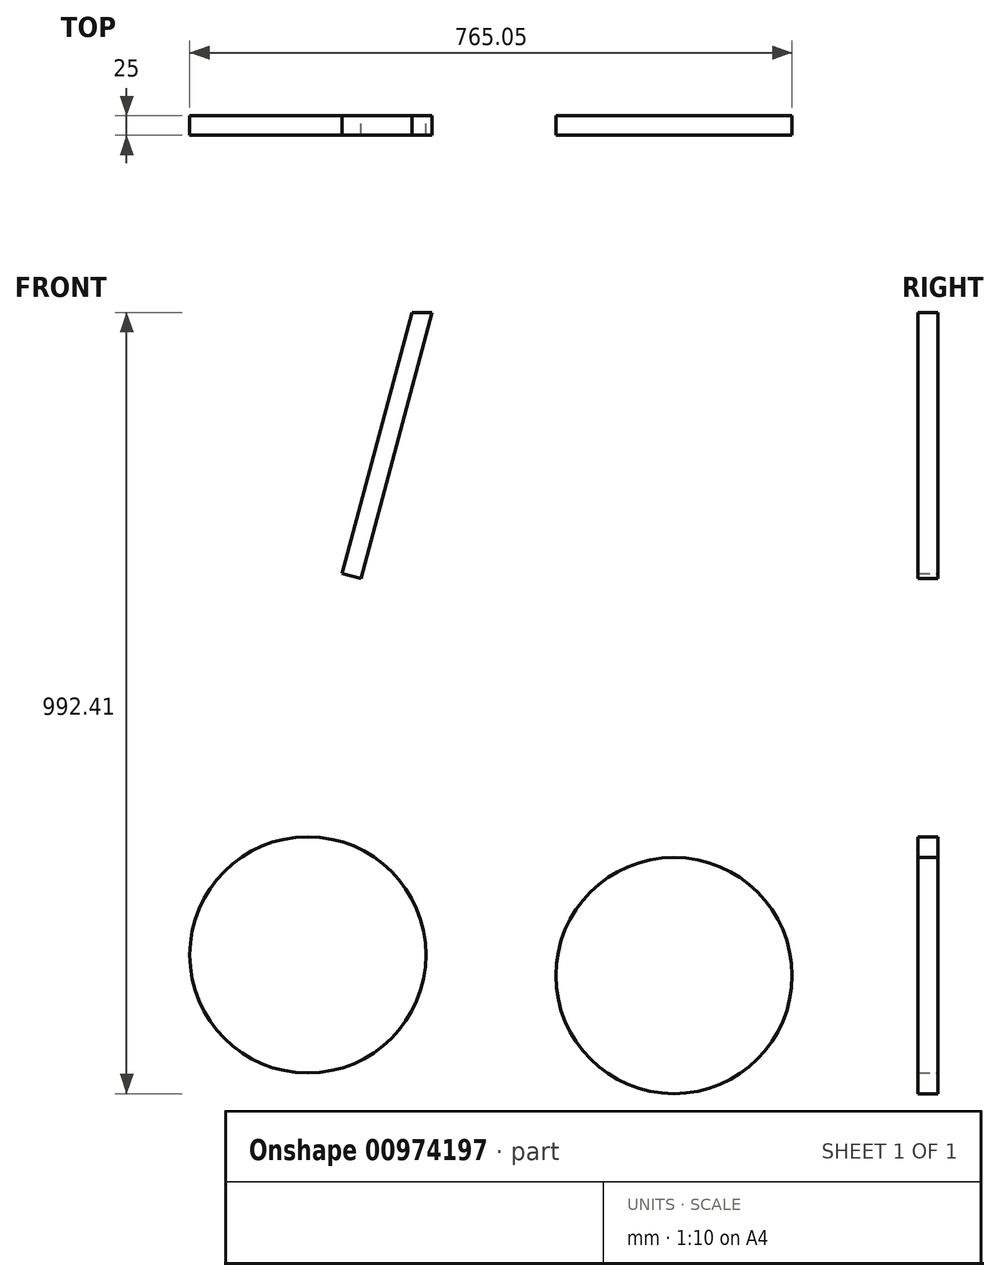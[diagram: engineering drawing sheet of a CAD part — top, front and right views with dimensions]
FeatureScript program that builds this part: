
annotation { "Feature Type Name" : "Feature", "Feature Type Description" : "" }
export const myFeature = defineFeature(function(context is Context, id is Id, definition is map)
    precondition{}
    {
        {
            var Q0;
            Q0=qCreatedBy(makeId("Front.planeOp"),FACE);
            var sketch = newSketch(context, id + "F0", { "sketchPlane" : qUnion([Q0])});
            skLineSegment(sketch, "E0", {"start": v(0, 0) * mm, "end": v(-150, 0) * mm, "construction": true});
            skLineSegment(sketch, "E1.bottom", {"start": v(-150, 0) * mm, "end": v(111.97, 0) * mm, "construction": true});
            skLineSegment(sketch, "E1.top", {"start": v(-150, 580) * mm, "end": v(111.97, 580) * mm, "construction": true});
            skLineSegment(sketch, "E2", {"start": v(257.6, 13.48) * mm, "end": v(377.86, 13.48) * mm, "construction": true});
            skLineSegment(sketch, "E3", {"start": v(377.86, 13.48) * mm, "end": v(357.95, -60.8) * mm, "construction": true});
            skLineSegment(sketch, "E4.0", {"start": v(353.7, 19.95) * mm, "end": v(333.8, -54.32) * mm});
            skLineSegment(sketch, "E5", {"start": v(351.97, 13.48) * mm, "end": v(351.97, 23.52) * mm, "construction": true});
            skLineSegment(sketch, "E6", {"start": v(111.97, 580) * mm, "end": v(44.64, 580) * mm, "construction": true});
            skLineSegment(sketch, "E7", {"start": v(-45.95, 241.93) * mm, "end": v(-70.1, 248.4) * mm});
            skLineSegment(sketch, "E8", {"start": v(18.76, 580) * mm, "end": v(44.64, 580) * mm});
            skLineSegment(sketch, "E9", {"start": v(-150, 580) * mm, "end": v(-50, 580) * mm, "construction": true});
            skLineSegment(sketch, "E10", {"start": v(-50, 580) * mm, "end": v(18.76, 580) * mm});
            skLineSegment(sketch, "E11", {"start": v(-45.95, 241.93) * mm, "end": v(-44.91, 245.79) * mm, "construction": true});
            skCircle(sketch, "E12", {"center": v(-89.64, -236.17) * mm, "radius": 150 * mm});
            skLineSegment(sketch, "E13", {"start": v(-89.64, -236.17) * mm, "end": v(-89.64, -346.17) * mm, "construction": true});
            skLineSegment(sketch, "E14", {"start": v(-191.62, -346.17) * mm, "end": v(12.34, -346.17) * mm, "construction": true});
            skLineSegment(sketch, "E15", {"start": v(111.97, 0) * mm, "end": v(111.97, 580) * mm, "construction": true});
            skPoint(sketch, "E16.orphan", {"position": v(150, 0) * mm});
            skPoint(sketch, "E17.orphan", {"position": v(150, 580) * mm});
            skLineSegment(sketch, "E18", {"start": v(111.97, 0) * mm, "end": v(-188.03, 0) * mm, "construction": true});
            skLineSegment(sketch, "E19", {"start": v(-188.03, 0) * mm, "end": v(-188.03, 580) * mm, "construction": true});
            skLineSegment(sketch, "E20", {"start": v(-188.03, 580) * mm, "end": v(111.97, 580) * mm, "construction": true});
            skLineSegment(sketch, "E21", {"start": v(-89.64, -346.17) * mm, "end": v(-89.64, -386.17) * mm, "construction": true});
            skCircle(sketch, "E22", {"center": v(375.41, -262.41) * mm, "radius": 150 * mm});
            skLineSegment(sketch, "E23", {"start": v(375.41, -262.41) * mm, "end": v(375.41, -112.41) * mm, "construction": true});
            skLineSegment(sketch, "E24", {"start": v(375.41, -262.41) * mm, "end": v(245.5, -337.41) * mm, "construction": true});
            skLineSegment(sketch, "E25", {"start": v(375.41, -262.41) * mm, "end": v(505.31, -337.41) * mm, "construction": true});
            skLineSegment(sketch, "E26", {"start": v(245.5, -337.41) * mm, "end": v(505.31, -337.41) * mm, "construction": true});
            skLineSegment(sketch, "E27", {"start": v(375.41, -337.41) * mm, "end": v(375.41, -412.41) * mm, "construction": true});
            skLineSegment(sketch, "E28", {"start": v(-89.64, -236.17) * mm, "end": v(-89.64, -86.17) * mm, "construction": true});
            skLineSegment(sketch, "E29", {"start": v(-89.64, -86.17) * mm, "end": v(-191.62, -346.17) * mm, "construction": true});
            skLineSegment(sketch, "E30", {"start": v(-89.64, -86.17) * mm, "end": v(12.34, -346.17) * mm, "construction": true});
            skLineSegment(sketch, "E31", {"start": v(245.5, -337.41) * mm, "end": v(375.41, -112.41) * mm, "construction": true});
            skLineSegment(sketch, "E32", {"start": v(375.41, -112.41) * mm, "end": v(505.31, -337.41) * mm, "construction": true});
            skLineSegment(sketch, "E33", {"start": v(-140.63, -216.17) * mm, "end": v(-229.28, -181.4) * mm, "construction": true});
            skLineSegment(sketch, "E34", {"start": v(-188.03, 0) * mm, "end": v(-113.03, 0) * mm, "construction": true});
            skLineSegment(sketch, "E35", {"start": v(-113.03, 0) * mm, "end": v(55.01, 627.12) * mm, "construction": true});
            skLineSegment(sketch, "E36.0", {"start": v(-88.88, -6.47) * mm, "end": v(79.16, 620.65) * mm, "construction": true});
            skLineSegment(sketch, "E37", {"start": v(68.27, 580) * mm, "end": v(-22.32, 241.93) * mm});
            skLineSegment(sketch, "E38", {"start": v(-22.32, 241.93) * mm, "end": v(-46.47, 248.4) * mm});
            skLineSegment(sketch, "E39", {"start": v(-46.47, 248.4) * mm, "end": v(42.38, 580) * mm});
            skLineSegment(sketch, "E40", {"start": v(42.38, 580) * mm, "end": v(68.27, 580) * mm});
            skLineSegment(sketch, "E41", {"start": v(-22.32, 241.93) * mm, "end": v(-21.29, 245.79) * mm, "construction": true});
            skLineSegment(sketch, "E42", {"start": v(-21.29, 245.79) * mm, "end": v(93.33, 0) * mm, "construction": true});
            skLineSegment(sketch, "E43.0", {"start": v(1.37, 256.36) * mm, "end": v(120.18, 1.57) * mm, "construction": true});
            skLineSegment(sketch, "E44", {"start": v(111.97, 0) * mm, "end": v(120.91, 0) * mm, "construction": true});
            skLineSegment(sketch, "E45", {"start": v(120.18, 1.57) * mm, "end": v(120.91, 0) * mm, "construction": true});
            skSolve(sketch);
        }
        {
            var Q0;
            Q0 = qSketchRegion(id + "F0", true);
            extrude(context, id + "F1", {"entities" : qUnion([Q0]), "depth" : 25 * mm, "offsetDistance" : 25 * mm});
        }
    });
